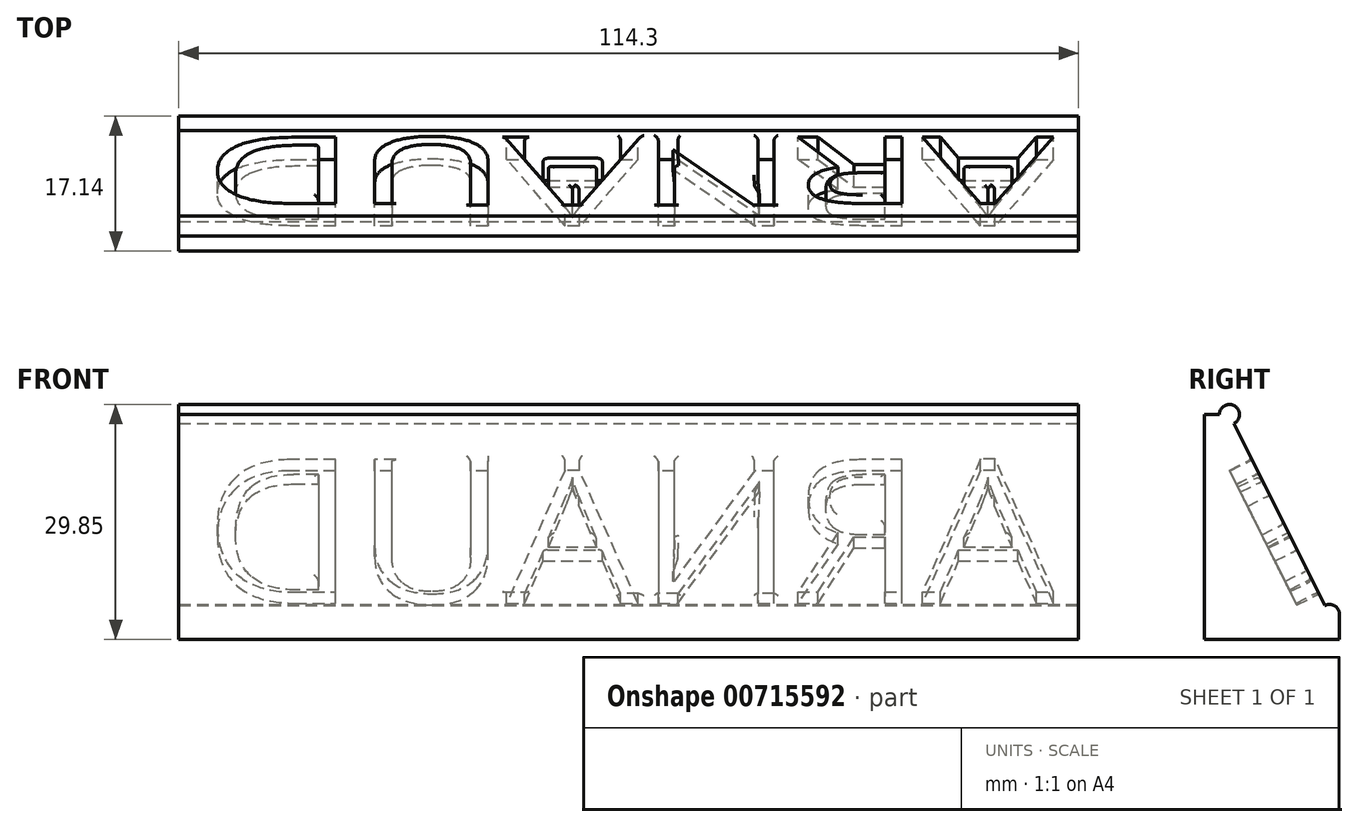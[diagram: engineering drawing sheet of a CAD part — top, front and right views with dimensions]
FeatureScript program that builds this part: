
annotation { "Feature Type Name" : "Feature", "Feature Type Description" : "" }
export const myFeature = defineFeature(function(context is Context, id is Id, definition is map)
    precondition{}
    {
        {
            var Q0;
            Q0=qCreatedBy(makeId("Right.planeOp"),FACE);
            var sketch = newSketch(context, id + "F0", { "sketchPlane" : qUnion([Q0])});
            skLineSegment(sketch, "E0", {"start": v(0, 0) * mm, "end": v(0, 25.4) * mm, "construction": true});
            skLineSegment(sketch, "E1", {"start": v(0, 25.4) * mm, "end": v(12.7, 0) * mm});
            skLineSegment(sketch, "E2", {"start": v(0, 0) * mm, "end": v(12.7, 0) * mm, "construction": true});
            skLineSegment(sketch, "E3", {"start": v(0, 25.4) * mm, "end": v(-3.17, 25.4) * mm});
            skLineSegment(sketch, "E4", {"start": v(-3.17, 25.4) * mm, "end": v(-3.17, 0) * mm});
            skLineSegment(sketch, "E5", {"start": v(-3.17, 0) * mm, "end": v(0, 0) * mm, "construction": true});
            skLineSegment(sketch, "E6", {"start": v(13.97, -3.17) * mm, "end": v(-3.17, -3.18) * mm});
            skLineSegment(sketch, "E7", {"start": v(-3.17, -3.18) * mm, "end": v(-3.17, 0) * mm});
            skCircle(sketch, "E8", {"center": v(0, 25.4) * mm, "radius": 1.27 * mm});
            skCircle(sketch, "E9", {"center": v(12.7, 0) * mm, "radius": 1.27 * mm});
            skLineSegment(sketch, "E10", {"start": v(13.97, 0) * mm, "end": v(13.97, -3.17) * mm});
            skSolve(sketch);
        }
        {
            var Q0;
            Q0 = qSketchRegion(id + "F0", true);
            extrude(context, id + "F1", {"entities" : qUnion([Q0]), "oppositeDirection" : true, "depth" : 114.3 * mm, "offsetDistance" : 25.4 * mm});
        }
        {
            var Q0;
            Q0=makeQuery(id+"F1.opExtrude","SWEPT_FACE",FACE,{"disambiguationData":[OSD([sQuery(id+"F0.wireOp",EDGE,"E1")])]});
            var sketch = newSketch(context, id + "F2", { "sketchPlane" : qUnion([Q0])});
            skText(sketch, "E11", { "text": "ARNAUD", "fontName": "OpenSans-Regular.ttf"});
            skLineSegment(sketch, "E12", {"start": v(0, -2.5) * mm, "end": v(114.3, -2.5) * mm, "construction": true});
            skLineSegment(sketch, "E13", {"start": v(3.18, -4.4) * mm, "end": v(3.18, -4.4) * mm});
            skLineSegment(sketch, "E14", {"start": v(111.13, -4.4) * mm, "end": v(111.13, -4.4) * mm});
            const initialGuessF2  = {"E11": [0.00317, -0.0025, 1, 0, 0.01896]};
            skSetInitialGuess(sketch, initialGuessF2);
            skSolve(sketch);
        }
        {
            var Q0;
            Q0 = qSketchRegion(id + "F2", true);
            extrude(context, id + "F3", {"entities" : qUnion([Q0]), "operationType" : NewBodyOperationType.REMOVE, "oppositeDirection" : true, "depth" : 3.17 * mm, "offsetDistance" : 25.4 * mm});
        }
        {
            var Q0;
            Q0=makeQuery(id+"F3.boolean.opBoolean","COPY",EDGE,{"derivedFrom":makeQuery(id+"F3.opExtrude","CAP_EDGE",EDGE,{"disambiguationData":[OSD([sQuery(id+"F2.wireOp",EDGE,"E11.sketch_text.stroke-43")])],"isStart":true})});
            var Q1;
            Q1=makeQuery(id+"F3.boolean.opBoolean","COPY",EDGE,{"derivedFrom":makeQuery(id+"F3.opExtrude","CAP_EDGE",EDGE,{"disambiguationData":[OSD([sQuery(id+"F2.wireOp",EDGE,"E11.sketch_text.stroke-45")])],"isStart":true})});
            var Q2;
            Q2=makeQuery(id+"F3.boolean.opBoolean","COPY",EDGE,{"derivedFrom":makeQuery(id+"F3.opExtrude","CAP_EDGE",EDGE,{"disambiguationData":[OSD([sQuery(id+"F2.wireOp",EDGE,"E11.sketch_text.stroke-42")])],"isStart":true})});
            var Q3;
            Q3=makeQuery(id+"F3.boolean.opBoolean","COPY",EDGE,{"derivedFrom":makeQuery(id+"F3.opExtrude","CAP_EDGE",EDGE,{"disambiguationData":[OSD([sQuery(id+"F2.wireOp",EDGE,"E11.sketch_text.stroke-41")])],"isStart":true})});
            var Q4;
            Q4=makeQuery(id+"F3.boolean.opBoolean","COPY",EDGE,{"derivedFrom":makeQuery(id+"F3.opExtrude","CAP_EDGE",EDGE,{"disambiguationData":[OSD([sQuery(id+"F2.wireOp",EDGE,"E11.sketch_text.stroke-39")])],"isStart":true})});
            var Q5;
            Q5=makeQuery(id+"F3.boolean.opBoolean","COPY",EDGE,{"derivedFrom":makeQuery(id+"F3.opExtrude","CAP_EDGE",EDGE,{"disambiguationData":[OSD([sQuery(id+"F2.wireOp",EDGE,"E11.sketch_text.stroke-32")])],"isStart":true})});
            var Q6;
            Q6=makeQuery(id+"F3.boolean.opBoolean","COPY",EDGE,{"derivedFrom":makeQuery(id+"F3.opExtrude","CAP_EDGE",EDGE,{"disambiguationData":[OSD([sQuery(id+"F2.wireOp",EDGE,"E11.sketch_text.stroke-31")])],"isStart":true})});
            var Q7;
            Q7=makeQuery(id+"F3.boolean.opBoolean","COPY",EDGE,{"derivedFrom":makeQuery(id+"F3.opExtrude","CAP_EDGE",EDGE,{"disambiguationData":[OSD([sQuery(id+"F2.wireOp",EDGE,"E11.sketch_text.stroke-44")])],"isStart":true})});
            var Q8;
            Q8=makeQuery(id+"F3.boolean.opBoolean","COPY",EDGE,{"derivedFrom":makeQuery(id+"F3.opExtrude","CAP_EDGE",EDGE,{"disambiguationData":[OSD([sQuery(id+"F2.wireOp",EDGE,"E11.sketch_text.stroke-38")])],"isStart":true})});
            var Q9;
            Q9=makeQuery(id+"F3.boolean.opBoolean","COPY",EDGE,{"derivedFrom":makeQuery(id+"F3.opExtrude","CAP_EDGE",EDGE,{"disambiguationData":[OSD([sQuery(id+"F2.wireOp",EDGE,"E11.sketch_text.stroke-37")])],"isStart":true})});
            var Q10;
            Q10=makeQuery(id+"F3.boolean.opBoolean","COPY",EDGE,{"derivedFrom":makeQuery(id+"F3.opExtrude","CAP_EDGE",EDGE,{"disambiguationData":[OSD([sQuery(id+"F2.wireOp",EDGE,"E11.sketch_text.stroke-34")])],"isStart":true})});
            var Q11;
            Q11=makeQuery(id+"F3.boolean.opBoolean","COPY",EDGE,{"derivedFrom":makeQuery(id+"F3.opExtrude","CAP_EDGE",EDGE,{"disambiguationData":[OSD([sQuery(id+"F2.wireOp",EDGE,"E11.sketch_text.stroke-35")])],"isStart":true})});
            var Q12;
            Q12=makeQuery(id+"F3.boolean.opBoolean","COPY",EDGE,{"derivedFrom":makeQuery(id+"F3.opExtrude","CAP_EDGE",EDGE,{"disambiguationData":[OSD([sQuery(id+"F2.wireOp",EDGE,"E11.sketch_text.stroke-36")])],"isStart":true})});
            var Q13;
            Q13=makeQuery(id+"F3.boolean.opBoolean","COPY",EDGE,{"derivedFrom":makeQuery(id+"F3.opExtrude","CAP_EDGE",EDGE,{"disambiguationData":[OSD([sQuery(id+"F2.wireOp",EDGE,"E11.sketch_text.stroke-49")])],"isStart":true})});
            var Q14;
            Q14=makeQuery(id+"F3.boolean.opBoolean","COPY",EDGE,{"derivedFrom":makeQuery(id+"F3.opExtrude","CAP_EDGE",EDGE,{"disambiguationData":[OSD([sQuery(id+"F2.wireOp",EDGE,"E11.sketch_text.stroke-50")])],"isStart":true})});
            var Q15;
            Q15=makeQuery(id+"F3.boolean.opBoolean","COPY",EDGE,{"derivedFrom":makeQuery(id+"F3.opExtrude","CAP_EDGE",EDGE,{"disambiguationData":[OSD([sQuery(id+"F2.wireOp",EDGE,"E11.sketch_text.stroke-48")])],"isStart":true})});
            var Q16;
            Q16=makeQuery(id+"F3.boolean.opBoolean","COPY",EDGE,{"derivedFrom":makeQuery(id+"F3.opExtrude","CAP_EDGE",EDGE,{"disambiguationData":[OSD([sQuery(id+"F2.wireOp",EDGE,"E11.sketch_text.stroke-58")])],"isStart":true})});
            var Q17;
            Q17=makeQuery(id+"F3.boolean.opBoolean","COPY",EDGE,{"derivedFrom":makeQuery(id+"F3.opExtrude","CAP_EDGE",EDGE,{"disambiguationData":[OSD([sQuery(id+"F2.wireOp",EDGE,"E11.sketch_text.stroke-54")])],"isStart":true})});
            var Q18;
            Q18=makeQuery(id+"F3.boolean.opBoolean","COPY",EDGE,{"derivedFrom":makeQuery(id+"F3.opExtrude","CAP_EDGE",EDGE,{"disambiguationData":[OSD([sQuery(id+"F2.wireOp",EDGE,"E11.sketch_text.stroke-55")])],"isStart":true})});
            var Q19;
            Q19=makeQuery(id+"F3.boolean.opBoolean","COPY",EDGE,{"derivedFrom":makeQuery(id+"F3.opExtrude","CAP_EDGE",EDGE,{"disambiguationData":[OSD([sQuery(id+"F2.wireOp",EDGE,"E11.sketch_text.stroke-57")])],"isStart":true})});
            var Q20;
            Q20=makeQuery(id+"F3.boolean.opBoolean","COPY",EDGE,{"derivedFrom":makeQuery(id+"F3.opExtrude","CAP_EDGE",EDGE,{"disambiguationData":[OSD([sQuery(id+"F2.wireOp",EDGE,"E11.sketch_text.stroke-51")])],"isStart":true})});
            var Q21;
            Q21=makeQuery(id+"F3.boolean.opBoolean","COPY",EDGE,{"derivedFrom":makeQuery(id+"F3.opExtrude","CAP_EDGE",EDGE,{"disambiguationData":[OSD([sQuery(id+"F2.wireOp",EDGE,"E11.sketch_text.stroke-52")])],"isStart":true})});
            var Q22;
            Q22=makeQuery(id+"F3.boolean.opBoolean","COPY",EDGE,{"derivedFrom":makeQuery(id+"F3.opExtrude","CAP_EDGE",EDGE,{"disambiguationData":[OSD([sQuery(id+"F2.wireOp",EDGE,"E11.sketch_text.stroke-65")])],"isStart":true})});
            var Q23;
            Q23=makeQuery(id+"F3.boolean.opBoolean","COPY",EDGE,{"derivedFrom":makeQuery(id+"F3.opExtrude","CAP_EDGE",EDGE,{"disambiguationData":[OSD([sQuery(id+"F2.wireOp",EDGE,"E11.sketch_text.stroke-66")])],"isStart":true})});
            var Q24;
            {var subQ0=sQuery(id+"F0.wireOp",EDGE,"E3");var subQ4=sQuery(id+"F0.wireOp",EDGE,"E1");Q24=makeQuery(id+"F3.boolean.opBoolean","SPLIT",FACE,{"disambiguationData":[TD([makeQuery(id+"F1.opExtrude","SWEPT_FACE",FACE,{"disambiguationData":[OSD([subQ0])]})])],"derivedFrom":makeQuery(id+"F1.opExtrude","SWEPT_FACE",FACE,{"disambiguationData":[OSD([subQ4])]})});}
            var Q25;
            Q25=makeQuery(id+"F3.boolean.opBoolean","COPY",EDGE,{"derivedFrom":makeQuery(id+"F3.opExtrude","CAP_EDGE",EDGE,{"disambiguationData":[OSD([sQuery(id+"F2.wireOp",EDGE,"E11.sketch_text.stroke-46")])],"isStart":true})});
            var Q26;
            Q26=makeQuery(id+"F3.boolean.opBoolean","SPLIT",FACE,{"disambiguationData":[TD([makeQuery(id+"F3.opExtrude","SWEPT_FACE",FACE,{"disambiguationData":[OSD([sQuery(id+"F2.wireOp",EDGE,"E11.sketch_text.stroke-80")])]})])],"derivedFrom":makeQuery(id+"F1.opExtrude","SWEPT_FACE",FACE,{"disambiguationData":[OSD([sQuery(id+"F0.wireOp",EDGE,"E1")])]})});
            var Q27;
            Q27=makeQuery(id+"F3.boolean.opBoolean","SPLIT",FACE,{"disambiguationData":[TD([makeQuery(id+"F3.opExtrude","SWEPT_FACE",FACE,{"disambiguationData":[OSD([sQuery(id+"F2.wireOp",EDGE,"E11.sketch_text.stroke-54")])]})])],"derivedFrom":makeQuery(id+"F1.opExtrude","SWEPT_FACE",FACE,{"disambiguationData":[OSD([sQuery(id+"F0.wireOp",EDGE,"E1")])]})});
            var Q28;
            Q28=makeQuery(id+"F3.boolean.opBoolean","SPLIT",FACE,{"disambiguationData":[TD([makeQuery(id+"F3.opExtrude","SWEPT_FACE",FACE,{"disambiguationData":[OSD([sQuery(id+"F2.wireOp",EDGE,"E11.sketch_text.stroke-24")])]})])],"derivedFrom":makeQuery(id+"F1.opExtrude","SWEPT_FACE",FACE,{"disambiguationData":[OSD([sQuery(id+"F0.wireOp",EDGE,"E1")])]})});
            var Q29;
            Q29=makeQuery(id+"F3.boolean.opBoolean","SPLIT",FACE,{"disambiguationData":[TD([makeQuery(id+"F3.opExtrude","SWEPT_FACE",FACE,{"disambiguationData":[OSD([sQuery(id+"F2.wireOp",EDGE,"E11.sketch_text.stroke-8")])]})])],"derivedFrom":makeQuery(id+"F1.opExtrude","SWEPT_FACE",FACE,{"disambiguationData":[OSD([sQuery(id+"F0.wireOp",EDGE,"E1")])]})});
            fillet(context, id + "F4", {"entities" : qUnion([Q0, Q1, Q2, Q3, Q4, Q5, Q6, Q7, Q8, Q9, Q10, Q11, Q12, Q13, Q14, Q15, Q16, Q17, Q18, Q19, Q20, Q21, Q22, Q23, Q24, Q25, Q26, Q27, Q28, Q29]), "radius" : 0.5 * mm, "tangentPropagation" : true, "allowEdgeOverflow" : false});
        }
    });
